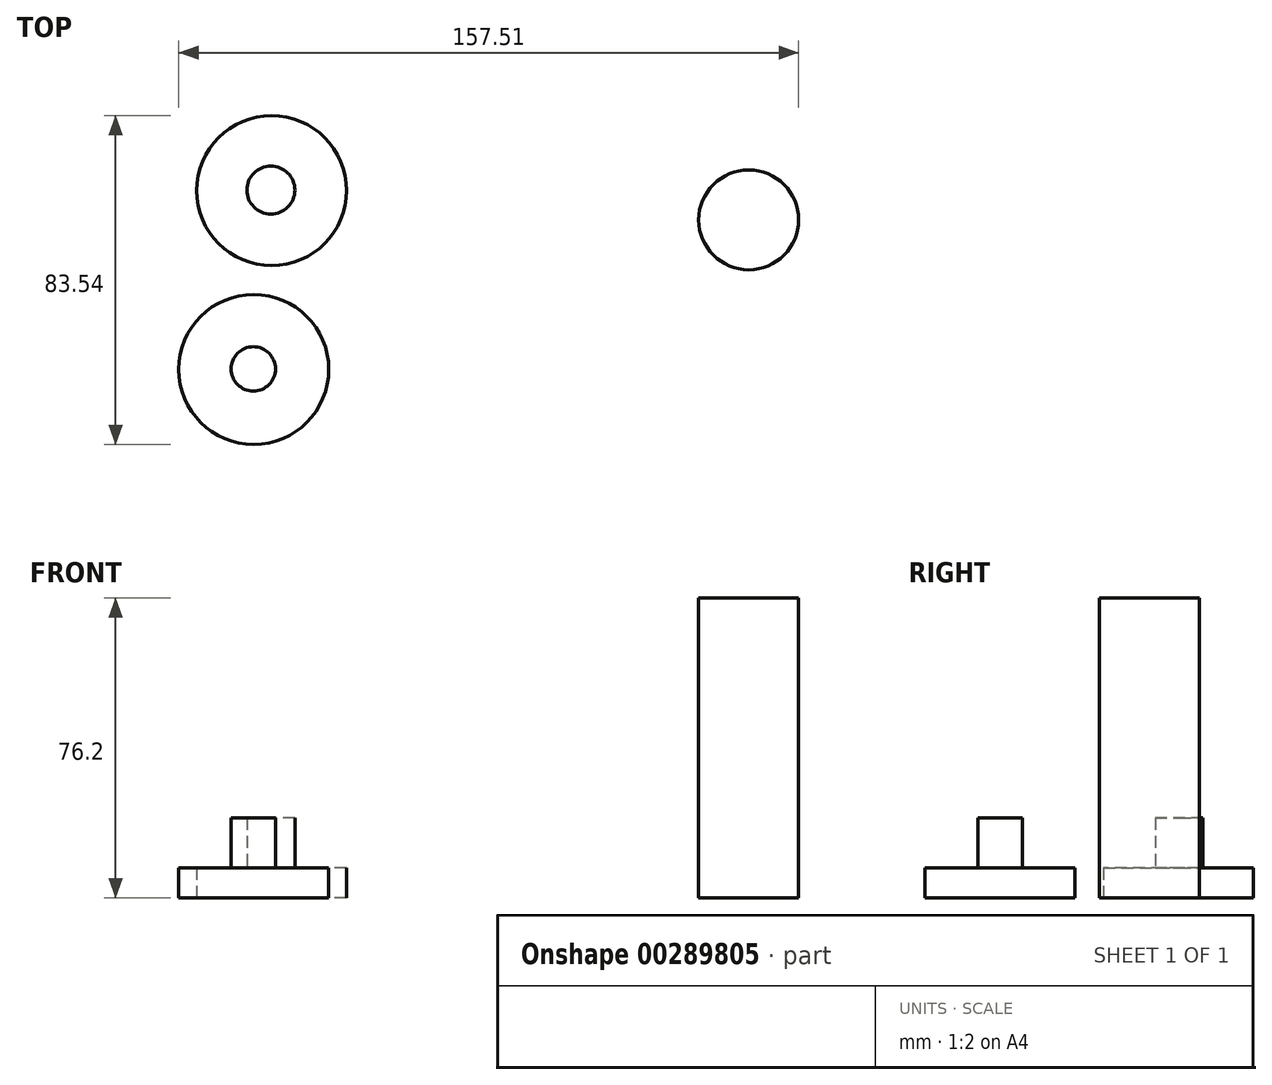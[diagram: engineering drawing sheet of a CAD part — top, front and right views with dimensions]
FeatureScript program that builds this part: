
annotation { "Feature Type Name" : "Feature", "Feature Type Description" : "" }
export const myFeature = defineFeature(function(context is Context, id is Id, definition is map)
    precondition{}
    {
        {
            var Q0;
            Q0=qCreatedBy(makeId("Top.planeOp"),FACE);
            var sketch = newSketch(context, id + "F0", { "sketchPlane" : qUnion([Q0])});
            skCircle(sketch, "E0", {"center": v(-121.2, 7.42) * mm, "radius": 19.05 * mm});
            skCircle(sketch, "E1", {"center": v(-125.76, -38.02) * mm, "radius": 19.05 * mm});
            skSolve(sketch);
        }
        {
            var Q0;
            Q0 = qSketchRegion(id + "F0", true);
            extrude(context, id + "F1", {"entities" : qUnion([Q0]), "depth" : 7.62 * mm});
        }
        {
            var Q0;
            Q0=qCreatedBy(makeId("Top.planeOp"),FACE);
            var sketch = newSketch(context, id + "F2", { "sketchPlane" : qUnion([Q0])});
            skCircle(sketch, "E2", {"center": v(0, 0) * mm, "radius": 12.7 * mm});
            skSolve(sketch);
        }
        {
            var Q0;
            Q0=makeQuery(id+"F2.imprint","IMPRINT",FACE,{"disambiguationData":[TD([[makeQuery(id+"F2.imprint","IMPRINT",EDGE,{"derivedFrom":sQuery(id+"F2.wireOp",EDGE,"E2")}),1.0]])]});
            extrude(context, id + "F3", {"entities" : qUnion([Q0]), "depth" : 76.2 * mm});
        }
        {
            var Q0;
            Q0=qCreatedBy(makeId("Top.planeOp"),FACE);
            cPlane(context, id + "F4", {"entities" : qUnion([Q0]), "cplaneType" : CPlaneType.OFFSET, "offset" : 7.62 * mm, "width" : 152.4 * mm, "height" : 152.4 * mm});
        }
        {
            var Q0;
            Q0=qCreatedBy(id+"F4.planeOp",FACE);
            var sketch = newSketch(context, id + "F5", { "sketchPlane" : qUnion([Q0])});
            skCircle(sketch, "E3", {"center": v(-121.4, 7.58) * mm, "radius": 6.1 * mm});
            skCircle(sketch, "E4", {"center": v(-125.86, -37.88) * mm, "radius": 5.63 * mm});
            skSolve(sketch);
        }
        {
            var Q0;
            Q0 = qSketchRegion(id + "F5", true);
            extrude(context, id + "F6", {"entities" : qUnion([Q0]), "depth" : 12.7 * mm});
        }
    });
